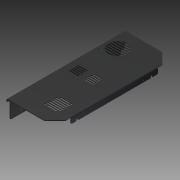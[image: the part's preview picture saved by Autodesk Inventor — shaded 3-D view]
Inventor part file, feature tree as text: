
AUTODESK INVENTOR PART (.ipt)
format: ipt  version: 2015 (Build 190159000, 159)  size: 855,040 bytes
history: native  units: mm
features: extrude x17, hole x7, fillet x5, other x2, shell x1, mirror x1, pattern_circular x1, pattern_linear x1
ambient origin geometry x8: Origin, YZ Plane, XZ Plane, XY Plane, X Axis, Y Axis, Z Axis, Center Point
bodies: Solid1 (feature_tree)
feature tree (35):
  extrude  "Extrusión1"  Depth=363.0mm
  fillet  "Empalme1"  Radius=150.0mm
  shell  "Vaciado1"  Thickness=60.0mm
  extrude  "Extrusión2"  Depth=3.0mm
  extrude  "Extrusión3"  Depth=1.5mm
  extrude  "Extrusión4"  Depth=25.0mm
  hole  "Agujero1"  [1 undecoded]
  extrude  "Extrusión5"  Depth=58.0mm TaperAngle=0.0deg
  fillet  "Empalme2"  Radius=20.0mm
  extrude  "Extrusión6"  Depth=58.0mm TaperAngle=0.0deg
  extrude  "Extrusión7"  Depth=10.0mm TaperAngle=0.0deg
  hole  "Agujero2"  [1 undecoded]
  extrude  "Extrusión9"  Depth=17.5mm
  extrude  "Extrusión10"  Depth=3.25mm
  mirror  "Simetría1"
  pattern_circular  "Patrón circular1"  [2 undecoded]
  extrude  "Extrusión11"  TaperAngle=30.0deg  [1 undecoded]
  extrude  "Extrusión12"  TaperAngle=30.0deg  [1 undecoded]
  pattern_linear  "Patrón rectangular1"  Spacing1=297.0mm  [1 undecoded]
  extrude  "Extrusión13"  Depth=8.5mm
  hole  "Agujero4"  [1 undecoded]
  extrude  "Extrusión14"  Depth=150.0mm
  fillet  "Empalme3"  Radius=44.0mm
  extrude  "Extrusión15"  Depth=5.0mm
  fillet  "Empalme4"  Radius=10.0mm
  extrude  "Extrusión16"  Depth=6.0mm
  fillet  "Empalme5"  Radius=4.0mm
  hole  "Agujero5"  [1 undecoded]
  other  "Desplazar cara1"
  hole  "Agujero6"  [1 undecoded]
  hole  "Agujero7"  [1 undecoded]
  extrude  "Extrusión17"  Depth=6.5mm
  extrude  "Extrusión18"  Depth=57.0mm
  other  "Definición1"
  hole  "Agujero3"  [1 undecoded]
note: 12 required parameter values undecoded (feature->parameter linkage not recoverable at this tier; creation-order binding heuristic only, values carry confidence <= 0.55)
